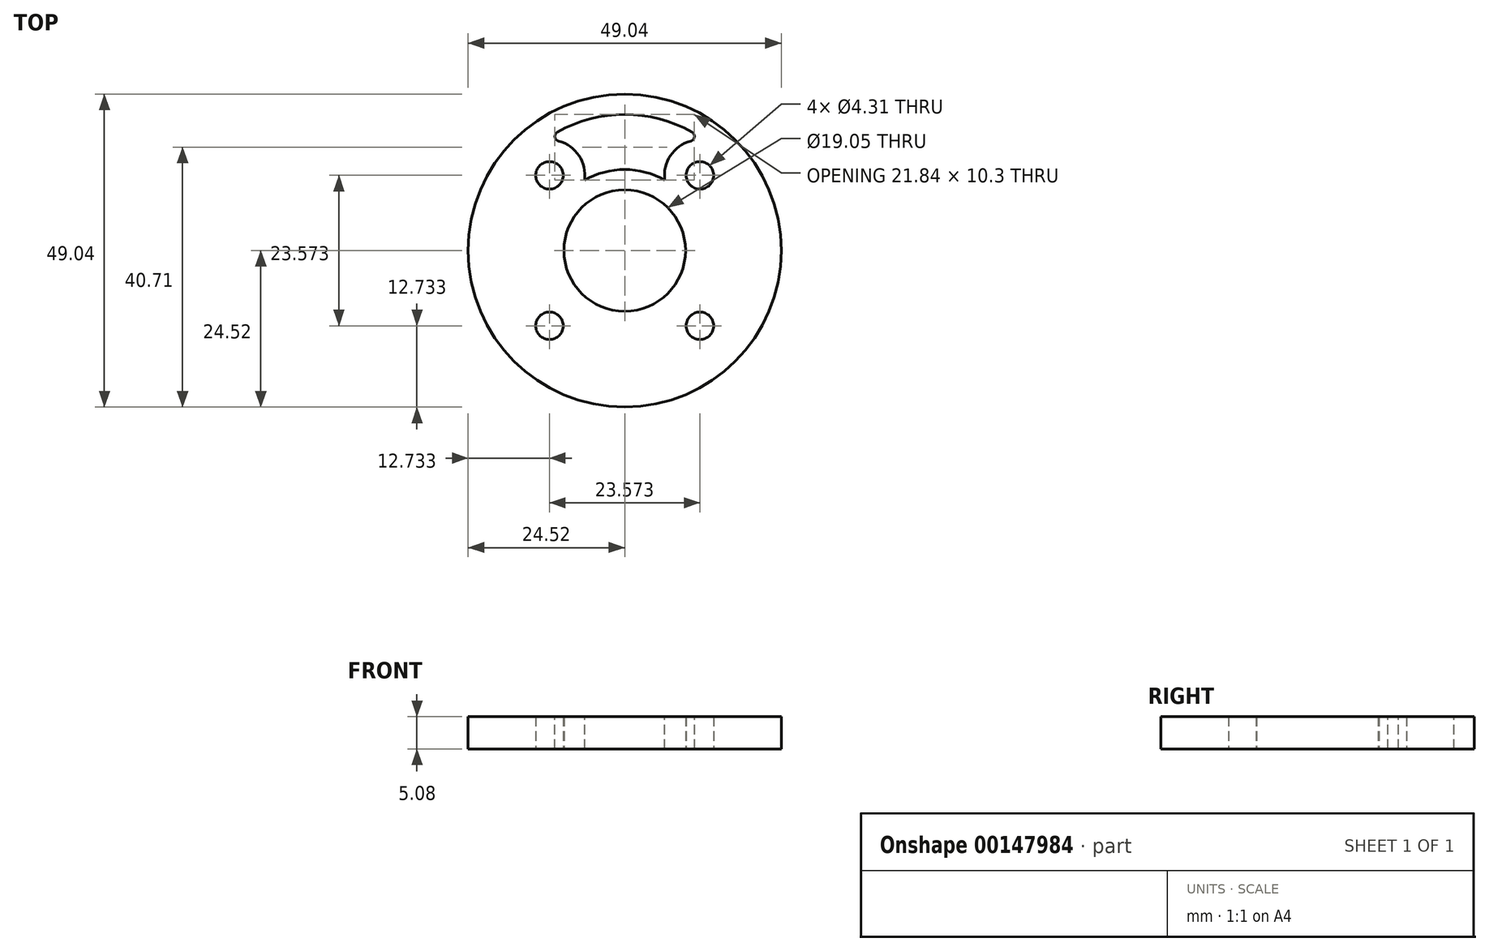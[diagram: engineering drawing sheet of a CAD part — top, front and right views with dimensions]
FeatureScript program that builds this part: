
annotation { "Feature Type Name" : "Feature", "Feature Type Description" : "" }
export const myFeature = defineFeature(function(context is Context, id is Id, definition is map)
    precondition{}
    {
        {
            var Q0;
            Q0=qCreatedBy(makeId("Top.planeOp"),FACE);
            var sketch = newSketch(context, id + "F0", { "sketchPlane" : qUnion([Q0])});
            skCircle(sketch, "E0", {"center": v(0, 0) * mm, "radius": 24.52 * mm});
            skCircle(sketch, "E1", {"center": v(0, 0) * mm, "radius": 9.53 * mm});
            skLineSegment(sketch, "E2.bottom", {"start": v(-11.79, 11.79) * mm, "end": v(11.79, 11.79) * mm, "construction": true});
            skLineSegment(sketch, "E2.top", {"start": v(-11.79, -11.79) * mm, "end": v(11.79, -11.79) * mm, "construction": true});
            skLineSegment(sketch, "E2.left", {"start": v(-11.79, 11.79) * mm, "end": v(-11.79, -11.79) * mm, "construction": true});
            skLineSegment(sketch, "E2.right", {"start": v(11.79, 11.79) * mm, "end": v(11.79, -11.79) * mm, "construction": true});
            skCircle(sketch, "E3", {"center": v(11.79, 11.79) * mm, "radius": 2.15 * mm});
            skCircle(sketch, "E4", {"center": v(-11.79, 11.79) * mm, "radius": 2.15 * mm});
            skCircle(sketch, "E5", {"center": v(-11.79, -11.79) * mm, "radius": 2.15 * mm});
            skCircle(sketch, "E6", {"center": v(11.79, -11.79) * mm, "radius": 2.15 * mm});
            skCircle(sketch, "E7", {"center": v(-11.79, -11.79) * mm, "radius": 3.97 * mm, "construction": true});
            skCircle(sketch, "E8", {"center": v(11.79, 11.79) * mm, "radius": 3.97 * mm, "construction": true});
            skSolve(sketch);
        }
        {
            var Q0;
            Q0=qSketchRegion(id+"F0",true);
            extrude(context, id + "F1", {"entities" : qUnion([Q0]), "depth" : 5.08 * mm});
        }
        {
            var Q0;
            Q0=makeQuery(id+"F1.opExtrude","CAP_FACE",FACE,{"disambiguationData":[OSD([sQuery(id+"F0.wireOp",EDGE,"E0"),sQuery(id+"F0.wireOp",EDGE,"E1"),sQuery(id+"F0.wireOp",EDGE,"E3"),sQuery(id+"F0.wireOp",EDGE,"E4"),sQuery(id+"F0.wireOp",EDGE,"E5"),sQuery(id+"F0.wireOp",EDGE,"E6")])],"isStart":false});
            var sketch = newSketch(context, id + "F2", { "sketchPlane" : qUnion([Q0])});
            skArc(sketch, "E9", {"start": v(-6.55, 9.92) * mm, "mid": v(-7.46, 15.27) * mm, "end": v(-12.5, 17.3) * mm});
            skArc(sketch, "E10", {"start": v(12.5, 17.3) * mm, "mid": v(7.46, 15.27) * mm, "end": v(6.55, 9.92) * mm});
            skArc(sketch, "E11", {"start": v(12.5, 17.3) * mm, "mid": v(0, 21.34) * mm, "end": v(-12.5, 17.3) * mm});
            skArc(sketch, "E12", {"start": v(7.14, 10.5) * mm, "mid": v(0, 12.7) * mm, "end": v(-7.14, 10.5) * mm});
            skLineSegment(sketch, "E13.bottom", {"start": v(-9.92, 6.55) * mm, "end": v(-6.55, 9.92) * mm, "construction": true});
            skLineSegment(sketch, "E13.top", {"start": v(-10.5, 7.14) * mm, "end": v(-7.14, 10.5) * mm, "construction": true});
            skLineSegment(sketch, "E13.left", {"start": v(-10.5, 7.14) * mm, "end": v(-9.92, 6.55) * mm, "construction": true});
            skLineSegment(sketch, "E13.right", {"start": v(-7.14, 10.5) * mm, "end": v(-6.55, 9.92) * mm});
            skLineSegment(sketch, "E14.bottom", {"start": v(9.92, 6.55) * mm, "end": v(6.55, 9.92) * mm, "construction": true});
            skLineSegment(sketch, "E14.top", {"start": v(10.5, 7.14) * mm, "end": v(7.14, 10.5) * mm, "construction": true});
            skLineSegment(sketch, "E14.left", {"start": v(10.5, 7.14) * mm, "end": v(9.92, 6.55) * mm, "construction": true});
            skLineSegment(sketch, "E14.right", {"start": v(7.14, 10.5) * mm, "end": v(6.55, 9.92) * mm});
            skLineSegment(sketch, "E15", {"start": v(-8.24, 8.24) * mm, "end": v(-11.79, 11.79) * mm, "construction": true});
            skLineSegment(sketch, "E16", {"start": v(-8.82, 8.82) * mm, "end": v(0, 0) * mm, "construction": true});
            skLineSegment(sketch, "E17", {"start": v(0, 0) * mm, "end": v(8.82, 8.82) * mm, "construction": true});
            skLineSegment(sketch, "E18", {"start": v(8.24, 8.24) * mm, "end": v(11.79, 11.79) * mm, "construction": true});
            skSolve(sketch);
        }
        {
            var Q0;
            Q0=makeQuery(id+"F2.imprint","IMPRINT",FACE,{"disambiguationData":[TD([[makeQuery(id+"F2.imprint","IMPRINT",EDGE,{"derivedFrom":sQuery(id+"F2.wireOp",EDGE,"E9")}),-1.0]])]});
            var Q1;
            Q1=makeQuery(id+"F1.opExtrude","CAP_FACE",FACE,{"disambiguationData":[OSD([sQuery(id+"F0.wireOp",EDGE,"E0"),sQuery(id+"F0.wireOp",EDGE,"E1"),sQuery(id+"F0.wireOp",EDGE,"E3"),sQuery(id+"F0.wireOp",EDGE,"E4"),sQuery(id+"F0.wireOp",EDGE,"E5"),sQuery(id+"F0.wireOp",EDGE,"E6")])],"isStart":true});
            extrude(context, id + "F3", {"entities" : qUnion([Q0]), "operationType" : NewBodyOperationType.REMOVE, "endBound" : BoundingType.UP_TO_SURFACE, "oppositeDirection" : true, "endBoundEntityFace" : qUnion([Q1]), "depth" : 25.4 * mm});
        }
        {
            var Q0;
            Q0=makeQuery(id+"F6MqURjXbY15YYN_1.1.F3.boolean.opBoolean","COPY",EDGE,{"derivedFrom":makeQuery(id+"F6MqURjXbY15YYN_1.1.F3.opExtrude","SWEPT_EDGE",EDGE,{"disambiguationData":[OSD([sQuery(id+"F2.wireOp",EDGE,"E9"),sQuery(id+"F2.wireOp",EDGE,"E11")])]})});
            var Q1;
            Q1=makeQuery(id+"F6MqURjXbY15YYN_1.1.F3.boolean.opBoolean","COPY",EDGE,{"derivedFrom":makeQuery(id+"F6MqURjXbY15YYN_1.1.F3.opExtrude","SWEPT_EDGE",EDGE,{"disambiguationData":[OSD([sQuery(id+"F2.wireOp",EDGE,"E10"),sQuery(id+"F2.wireOp",EDGE,"E11")])]})});
            var Q2;
            Q2=makeQuery(id+"F6MqURjXbY15YYN_1.2.F3.boolean.opBoolean","COPY",EDGE,{"derivedFrom":makeQuery(id+"F6MqURjXbY15YYN_1.2.F3.opExtrude","SWEPT_EDGE",EDGE,{"disambiguationData":[OSD([sQuery(id+"F2.wireOp",EDGE,"E9"),sQuery(id+"F2.wireOp",EDGE,"E11")])]})});
            var Q3;
            Q3=makeQuery(id+"F6MqURjXbY15YYN_1.2.F3.boolean.opBoolean","COPY",EDGE,{"derivedFrom":makeQuery(id+"F6MqURjXbY15YYN_1.2.F3.opExtrude","SWEPT_EDGE",EDGE,{"disambiguationData":[OSD([sQuery(id+"F2.wireOp",EDGE,"E10"),sQuery(id+"F2.wireOp",EDGE,"E11")])]})});
            var Q4;
            Q4=makeQuery(id+"F6MqURjXbY15YYN_1.3.F3.boolean.opBoolean","COPY",EDGE,{"derivedFrom":makeQuery(id+"F6MqURjXbY15YYN_1.3.F3.opExtrude","SWEPT_EDGE",EDGE,{"disambiguationData":[OSD([sQuery(id+"F2.wireOp",EDGE,"E9"),sQuery(id+"F2.wireOp",EDGE,"E11")])]})});
            var Q5;
            Q5=makeQuery(id+"F6MqURjXbY15YYN_1.3.F3.boolean.opBoolean","COPY",EDGE,{"derivedFrom":makeQuery(id+"F6MqURjXbY15YYN_1.3.F3.opExtrude","SWEPT_EDGE",EDGE,{"disambiguationData":[OSD([sQuery(id+"F2.wireOp",EDGE,"E10"),sQuery(id+"F2.wireOp",EDGE,"E11")])]})});
            var Q6;
            Q6=makeQuery(id+"F3.boolean.opBoolean","COPY",EDGE,{"derivedFrom":makeQuery(id+"F3.opExtrude","SWEPT_EDGE",EDGE,{"disambiguationData":[OSD([sQuery(id+"F2.wireOp",EDGE,"E9"),sQuery(id+"F2.wireOp",EDGE,"E11")])]})});
            var Q7;
            Q7=makeQuery(id+"F3.boolean.opBoolean","COPY",EDGE,{"derivedFrom":makeQuery(id+"F3.opExtrude","SWEPT_EDGE",EDGE,{"disambiguationData":[OSD([sQuery(id+"F2.wireOp",EDGE,"E10"),sQuery(id+"F2.wireOp",EDGE,"E11")])]})});
            fillet(context, id + "F4", {"entities" : qUnion([Q0, Q1, Q2, Q3, Q4, Q5, Q6, Q7]), "radius" : 0.76 * mm, "tangentPropagation" : true, "allowEdgeOverflow" : false});
        }
    });
